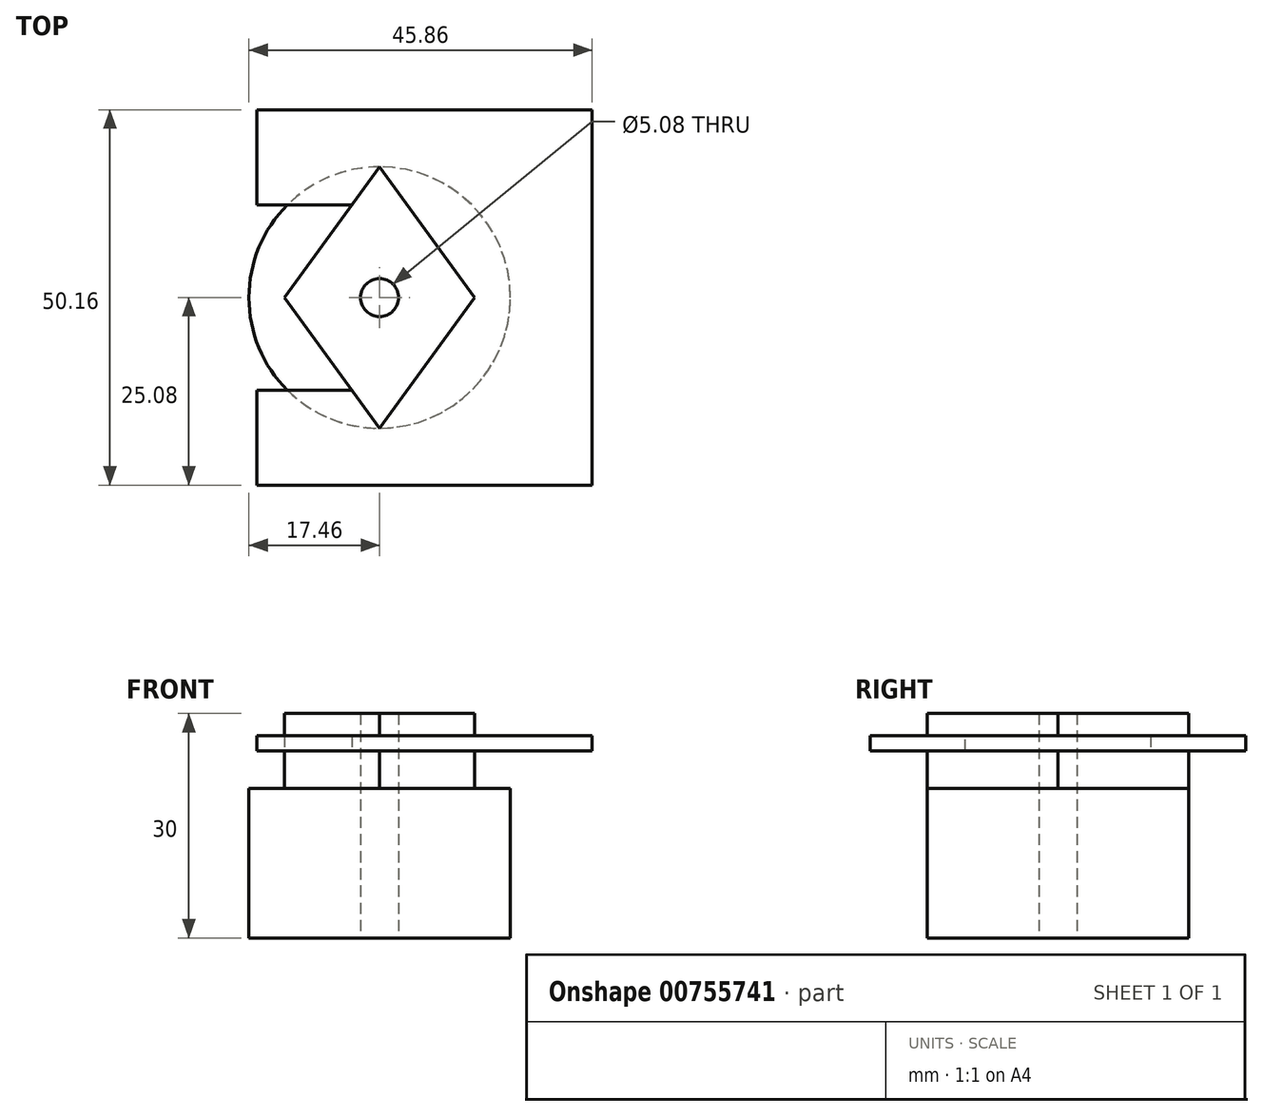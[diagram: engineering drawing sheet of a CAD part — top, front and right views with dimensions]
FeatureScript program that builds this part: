
annotation { "Feature Type Name" : "Feature", "Feature Type Description" : "" }
export const myFeature = defineFeature(function(context is Context, id is Id, definition is map)
    precondition{}
    {
        {
            var Q0;
            Q0=qCreatedBy(makeId("Top.planeOp"),FACE);
            var sketch = newSketch(context, id + "F0", { "sketchPlane" : qUnion([Q0])});
            skCircle(sketch, "E0", {"center": v(0, 0) * mm, "radius": 2.54 * mm});
            skCircle(sketch, "E1", {"center": v(0, 0) * mm, "radius": 17.46 * mm});
            skLineSegment(sketch, "E2", {"start": v(0, 0) * mm, "end": v(-12.7, 0) * mm, "construction": true});
            skLineSegment(sketch, "E3", {"start": v(0, 0) * mm, "end": v(0, 17.46) * mm, "construction": true});
            skLineSegment(sketch, "E4", {"start": v(0, 17.46) * mm, "end": v(-12.7, 0) * mm});
            skLineSegment(sketch, "E5.MirrorCS", {"start": v(0, -17.46) * mm, "end": v(-12.7, 0) * mm});
            skLineSegment(sketch, "E6.MirrorCS", {"start": v(0, -17.46) * mm, "end": v(12.7, 0) * mm});
            skLineSegment(sketch, "E7.MirrorCS", {"start": v(0, 17.46) * mm, "end": v(12.7, 0) * mm});
            skSolve(sketch);
        }
        {
            var Q0;
            Q0=makeQuery(id+"F0.imprint","IMPRINT",FACE,{"disambiguationData":[TD([[makeQuery(id+"F0.imprint","IMPRINT",EDGE,{"derivedFrom":sQuery(id+"F0.wireOp",EDGE,"E0")}),-1.0]])]});
            var Q1;
            {var subQ2=sQuery(id+"F0.wireOp",EDGE,"E6.MirrorCS");Q1=makeQuery(id+"F0.imprint","IMPRINT",FACE,{"disambiguationData":[TD([[makeQuery(id+"F0.imprint","IMPRINT",EDGE,{"derivedFrom":subQ2}),-1.0]])]});}
            var Q2;
            {var subQ0=sQuery(id+"F0.wireOp",EDGE,"E4");Q2=makeQuery(id+"F0.imprint","IMPRINT",FACE,{"disambiguationData":[TD([[makeQuery(id+"F0.imprint","IMPRINT",EDGE,{"derivedFrom":subQ0}),-1.0]])]});}
            extrude(context, id + "F1", {"entities" : qUnion([Q0, Q1, Q2]), "depth" : 20 * mm, "offsetDistance" : 25.4 * mm});
        }
        {
            var Q0;
            Q0=makeQuery(id+"F0.imprint","IMPRINT",FACE,{"disambiguationData":[TD([[makeQuery(id+"F0.imprint","IMPRINT",EDGE,{"derivedFrom":sQuery(id+"F0.wireOp",EDGE,"E0")}),-1.0]])]});
            extrude(context, id + "F2", {"entities" : qUnion([Q0]), "operationType" : NewBodyOperationType.ADD, "depth" : 30 * mm, "offsetDistance" : 25.4 * mm});
        }
        {
            var Q0;
            Q0=qCreatedBy(makeId("Right.planeOp"),FACE);
            var sketch = newSketch(context, id + "F3", { "sketchPlane" : qUnion([Q0])});
            skLineSegment(sketch, "E8.top", {"start": v(17.46, 27) * mm, "end": v(-17.46, 27) * mm});
            skLineSegment(sketch, "E8.left", {"start": v(17.46, 25) * mm, "end": v(17.46, 27) * mm});
            skLineSegment(sketch, "E8.right", {"start": v(-17.46, 25) * mm, "end": v(-17.46, 27) * mm});
            skLineSegment(sketch, "E9", {"start": v(-12.38, 27) * mm, "end": v(-12.38, 25) * mm});
            skLineSegment(sketch, "E10.MirrorCS", {"start": v(12.38, 27) * mm, "end": v(12.38, 25) * mm});
            skLineSegment(sketch, "E11", {"start": v(17.46, 25) * mm, "end": v(-17.46, 25) * mm});
            skLineSegment(sketch, "E12", {"start": v(-17.46, 27) * mm, "end": v(-17.46, 25) * mm});
            skSolve(sketch);
        }
        {
            var Q0;
            {var subQ0=sQuery(id+"F3.wireOp",EDGE,"E8.left");Q0=makeQuery(id+"F3.imprint","IMPRINT",FACE,{"disambiguationData":[TD([[makeQuery(id+"F3.imprint","IMPRINT",EDGE,{"derivedFrom":subQ0}),1.0]])]});}
            var Q1;
            {var subQ0=sQuery(id+"F3.wireOp",EDGE,"E9");Q1=makeQuery(id+"F3.imprint","IMPRINT",FACE,{"disambiguationData":[TD([[makeQuery(id+"F3.imprint","IMPRINT",EDGE,{"derivedFrom":subQ0}),1.0]])]});}
            var Q2;
            {var subQ2=sQuery(id+"F3.wireOp",EDGE,"E9");Q2=makeQuery(id+"F3.imprint","IMPRINT",FACE,{"disambiguationData":[TD([[makeQuery(id+"F3.imprint","IMPRINT",EDGE,{"derivedFrom":subQ2}),-1.0]])]});}
            extrude(context, id + "F4", {"entities" : qUnion([Q0, Q1, Q2]), "operationType" : NewBodyOperationType.REMOVE, "depth" : 25.4 * mm, "offsetDistance" : 25.4 * mm, "hasSecondDirection" : true, "secondDirectionOppositeDirection" : false, "secondDirectionDepth" : 3 * mm});
        }
        {
            var Q0;
            {var subQ2=sQuery(id+"F3.wireOp",EDGE,"E9");Q0=makeQuery(id+"F3.imprint","IMPRINT",FACE,{"disambiguationData":[TD([[makeQuery(id+"F3.imprint","IMPRINT",EDGE,{"derivedFrom":subQ2}),-1.0]])]});}
            var Q1;
            {var subQ0=sQuery(id+"F3.wireOp",EDGE,"E8.left");Q1=makeQuery(id+"F3.imprint","IMPRINT",FACE,{"disambiguationData":[TD([[makeQuery(id+"F3.imprint","IMPRINT",EDGE,{"derivedFrom":subQ0}),1.0]])]});}
            extrude(context, id + "F5", {"entities" : qUnion([Q0, Q1]), "operationType" : NewBodyOperationType.REMOVE, "endBound" : BoundingType.SYMMETRIC, "oppositeDirection" : true, "depth" : 25.4 * mm, "offsetDistance" : 25.4 * mm});
        }
        {
            var Q0;
            Q0=makeQuery(id+"F4.boolean.opBoolean","COPY",FACE,{"derivedFrom":makeQuery(id+"F4.opExtrude","CAP_FACE",FACE,{"disambiguationData":[OSD([sQuery(id+"F3.wireOp",EDGE,"E8.bottom"),sQuery(id+"F3.wireOp",EDGE,"E8.top"),sQuery(id+"F3.wireOp",EDGE,"E8.left"),sQuery(id+"F3.wireOp",EDGE,"E8.right")])],"isStart":true})});
            extrude(context, id + "F6", {"entities" : qUnion([Q0]), "depth" : 25.4 * mm, "offsetDistance" : 25.4 * mm});
        }
        {
            var Q0;
            Q0=makeQuery(id+"F6.opExtrude","SWEPT_FACE",FACE,{"disambiguationData":[OSD([sQuery(id+"F3.wireOp",EDGE,"E8.bottom"),sQuery(id+"F3.wireOp",EDGE,"E8.top"),sQuery(id+"F3.wireOp",EDGE,"E8.left"),sQuery(id+"F3.wireOp",EDGE,"E8.right"),sQuery(id+"F3.wireOp",EDGE,"E9")])]});
            var Q1;
            Q1=makeQuery(id+"F5.boolean.opBoolean","COPY",FACE,{"derivedFrom":makeQuery(id+"F5.opExtrude","SWEPT_FACE",FACE,{"disambiguationData":[OSD([sQuery(id+"F3.wireOp",EDGE,"E9")])]})});
            extrude(context, id + "F7", {"entities" : qUnion([Q0, Q1]), "operationType" : NewBodyOperationType.ADD, "depth" : 12.7 * mm, "offsetDistance" : 25.4 * mm});
        }
        {
            var Q0;
            Q0=makeQuery(id+"F5.boolean.opBoolean","COPY",FACE,{"derivedFrom":makeQuery(id+"F5.opExtrude","SWEPT_FACE",FACE,{"disambiguationData":[OSD([sQuery(id+"F3.wireOp",EDGE,"E10.MirrorCS")])]})});
            var Q1;
            Q1=makeQuery(id+"F6.opExtrude","SWEPT_FACE",FACE,{"disambiguationData":[OSD([sQuery(id+"F3.wireOp",EDGE,"E8.bottom"),sQuery(id+"F3.wireOp",EDGE,"E8.top"),sQuery(id+"F3.wireOp",EDGE,"E8.left"),sQuery(id+"F3.wireOp",EDGE,"E8.right"),sQuery(id+"F3.wireOp",EDGE,"E10.MirrorCS")])]});
            extrude(context, id + "F8", {"entities" : qUnion([Q0, Q1]), "operationType" : NewBodyOperationType.ADD, "depth" : 12.7 * mm, "offsetDistance" : 25.4 * mm});
        }
        {
            var Q0;
            Q0=makeQuery(id+"F8.opExtrude","SWEPT_FACE",FACE,{"disambiguationData":[OSD([sQuery(id+"F0.wireOp",EDGE,"E4"),sQuery(id+"F3.wireOp",EDGE,"E10.MirrorCS")])]});
            var Q1;
            Q1=makeQuery(id+"F7.opExtrude","SWEPT_FACE",FACE,{"disambiguationData":[OSD([sQuery(id+"F0.wireOp",EDGE,"E5.MirrorCS"),sQuery(id+"F3.wireOp",EDGE,"E9")])]});
            extrude(context, id + "F9", {"entities" : qUnion([Q0, Q1]), "operationType" : NewBodyOperationType.ADD, "depth" : 12.7 * mm, "offsetDistance" : 25.4 * mm});
        }
    });
